# Revit family: FU_Ottoman_Wudi_8-1
name_source: partatom
category: Furniture
units: mm (PartAtom-declared; Revit-internal decimal feet)

## family parameters
Always vertical = Yes
Cut with Voids When Loaded = No
OmniClass Number = 23.40.20.00
OmniClass Title = General Furniture and Specialties
Room Calculation Point = No
Shared = No
Work Plane-Based = No

## types (1)
- Wudi 8.1
    Default Elevation = 0 mm  [stored 0 ft]
    Depth = 470 mm  [stored 1.54199 ft]
    Description = Upholstered ottoman with solid oak frame. 60 x 45cm
    Frame = Wood - Oak - Natural - V
    Height = 410 mm  [stored 1.34514 ft]
    Manufacturer = Sandler
    Model = Wudi 8.1
    Seat = Fabric - Gravity - Wheat CPC21
    URL = https://www.sandlerseating.com
    Width = 610 mm  [stored 2.00131 ft]

note: [stored X ft] marks values corroborated as IEEE doubles in the binary element streams (Revit-internal decimal feet)

## geometry (parser evidence)
native form markers: Sweep x3
no freeform markers — native parametric forms only
